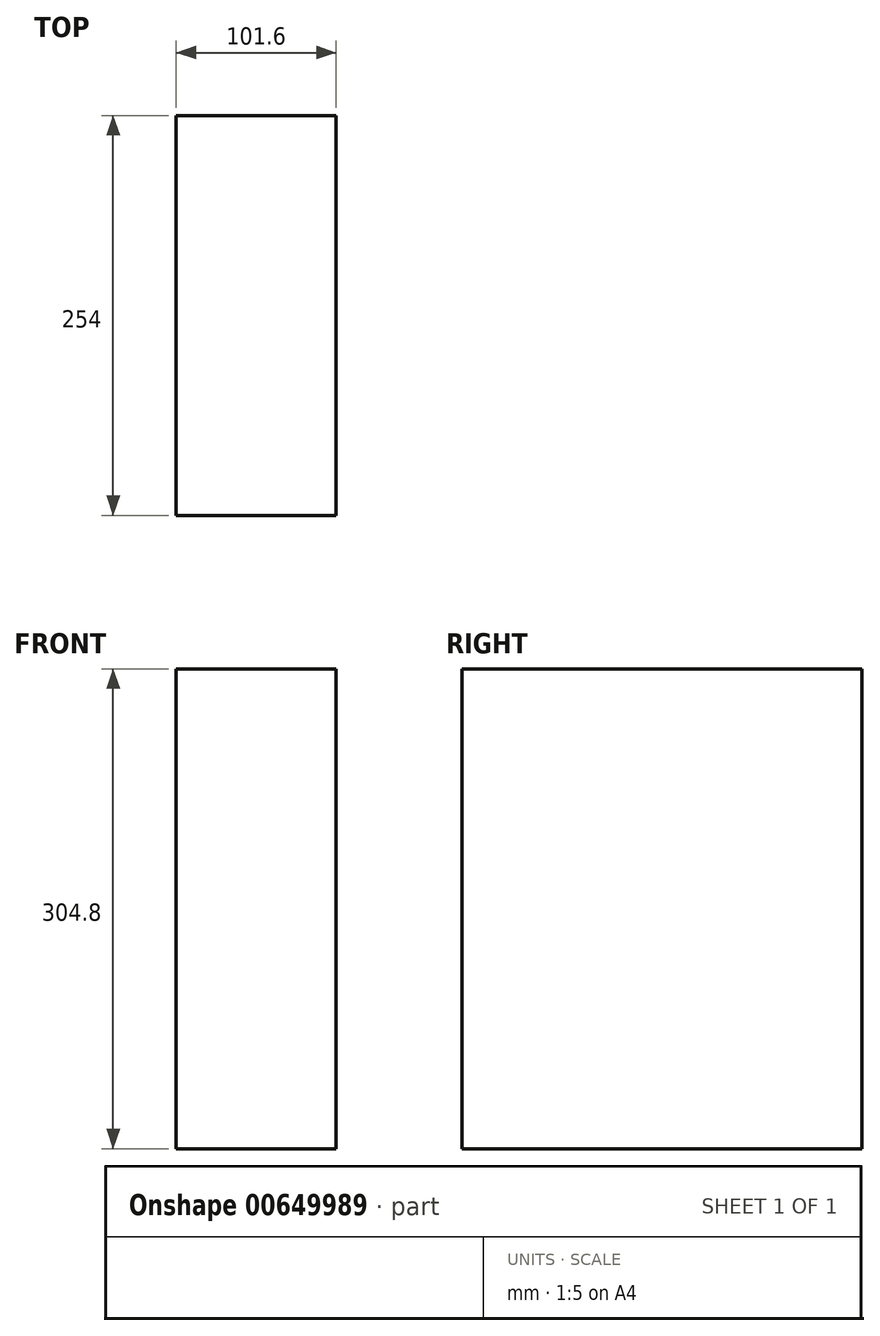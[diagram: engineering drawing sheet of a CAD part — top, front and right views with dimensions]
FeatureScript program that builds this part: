
annotation { "Feature Type Name" : "Feature", "Feature Type Description" : "" }
export const myFeature = defineFeature(function(context is Context, id is Id, definition is map)
    precondition{}
    {
        {
            var Q0;
            Q0=qCreatedBy(makeId("Front.planeOp"),FACE);
            var sketch = newSketch(context, id + "F0", { "sketchPlane" : qUnion([Q0])});
            skLineSegment(sketch, "E0.bottom", {"start": v(50.8, 152.4) * mm, "end": v(-50.8, 152.4) * mm});
            skLineSegment(sketch, "E0.top", {"start": v(50.8, -152.4) * mm, "end": v(-50.8, -152.4) * mm});
            skLineSegment(sketch, "E0.left", {"start": v(50.8, 152.4) * mm, "end": v(50.8, -152.4) * mm});
            skLineSegment(sketch, "E0.right", {"start": v(-50.8, 152.4) * mm, "end": v(-50.8, -152.4) * mm});
            skPoint(sketch, "E0.middle", {"position": v(0, 0) * mm});
            skSolve(sketch);
        }
        {
            var Q0;
            Q0=makeQuery(id+"F0.imprint","IMPRINT",FACE,{"disambiguationData":[TD([[makeQuery(id+"F0.imprint","IMPRINT",EDGE,{"derivedFrom":sQuery(id+"F0.wireOp",EDGE,"E0.bottom")}),1.0]])]});
            extrude(context, id + "F1", {"entities" : qUnion([Q0]), "endBound" : BoundingType.SYMMETRIC, "depth" : 254 * mm, "offsetDistance" : 25.4 * mm});
        }
    });
